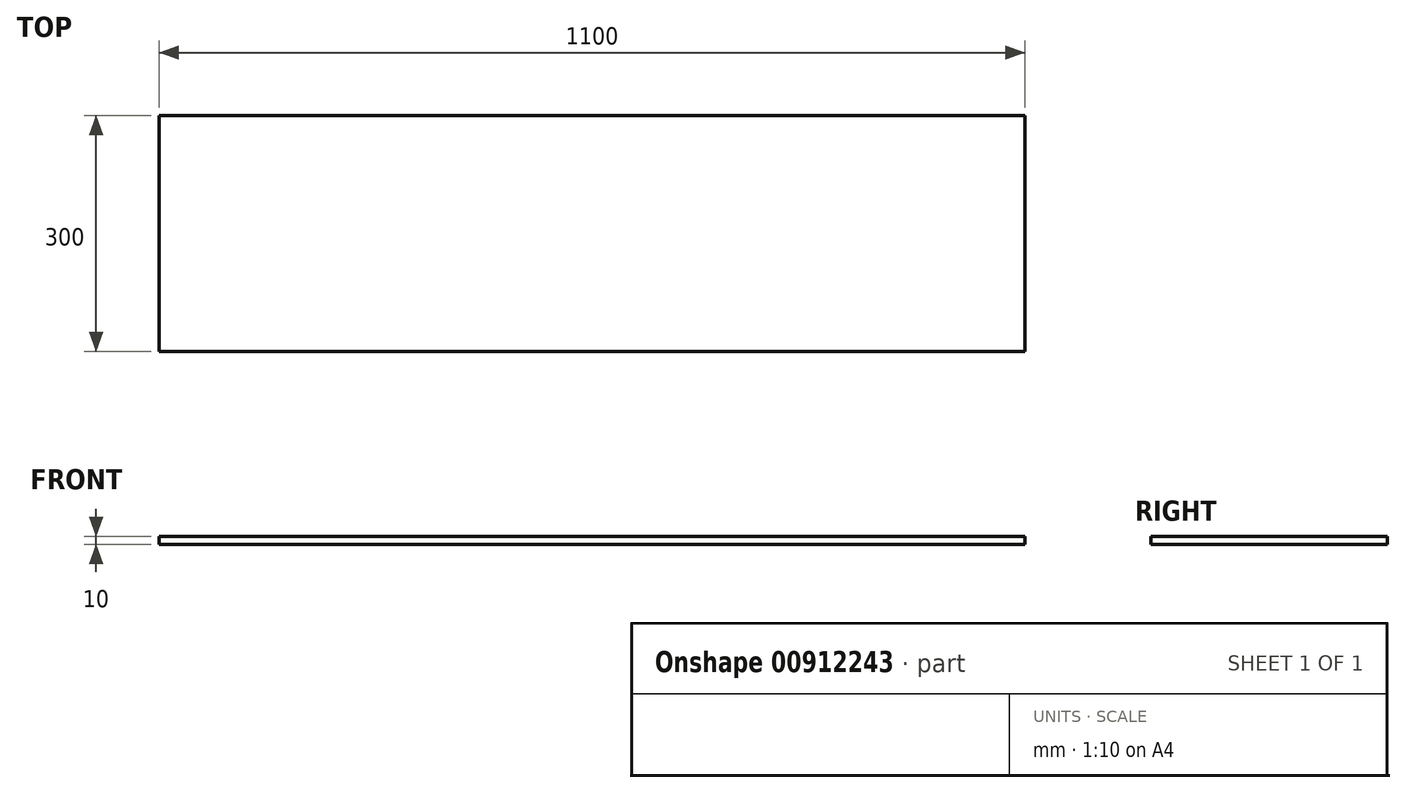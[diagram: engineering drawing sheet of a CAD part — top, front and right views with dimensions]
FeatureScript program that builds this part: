
annotation { "Feature Type Name" : "Feature", "Feature Type Description" : "" }
export const myFeature = defineFeature(function(context is Context, id is Id, definition is map)
    precondition{}
    {
        {
            var Q0;
            Q0=qCreatedBy(makeId("Top.planeOp"),FACE);
            var sketch = newSketch(context, id + "F0", { "sketchPlane" : qUnion([Q0])});
            skLineSegment(sketch, "E0.bottom", {"start": v(-408.39, 79.84) * mm, "end": v(691.61, 79.84) * mm});
            skLineSegment(sketch, "E0.top", {"start": v(-408.39, -220.16) * mm, "end": v(691.61, -220.16) * mm});
            skLineSegment(sketch, "E0.left", {"start": v(-408.39, 79.84) * mm, "end": v(-408.39, -220.16) * mm});
            skLineSegment(sketch, "E0.right", {"start": v(691.61, 79.84) * mm, "end": v(691.61, -220.16) * mm});
            skSolve(sketch);
        }
        {
            var Q0;
            Q0=makeQuery(id+"F0.imprint","IMPRINT",FACE,{"disambiguationData":[TD([[makeQuery(id+"F0.imprint","IMPRINT",EDGE,{"derivedFrom":sQuery(id+"F0.wireOp",EDGE,"E0.bottom")}),-1.0]])]});
            extrude(context, id + "F1", {"entities" : qUnion([Q0]), "depth" : 10 * mm, "offsetDistance" : 25 * mm});
        }
    });
